# Revit family: Rinnai VT26  - face based
name_source: partatom
category: Plumbing Fixtures
revit_build: Autodesk Revit 2018 (Build: 20170223_1515(x64)
units: mm (PartAtom-declared; Revit-internal decimal feet)

## family parameters
Cut with Voids When Loaded = No
Host = Face
Part Type = Normal
Room Calculation Point = No
Round Connector Dimension = Use Diameter
Shared = No

## types (1)
- Rinnai VT26 External
    230 volt supply = 230 V
    CW Connection = Yes
    Cold Water Connection = Cold Water
    Cost = 1779 $
    Default Elevation = 1219 mm
    Description = Gas Califont Water Heater
    Gas Flow = 0.0 L/s
    Gas Supply Connection = Gas Supply - Copper
    HW Connection = Yes
    Hot Water Conection = Hot Water Out
    Keynote = 71-21
    Manufacturer = Rinnai
    Model = Infinity VT26  External
    Model Data = Colour       White
Input:       199 MJ/h or 55 kW
Output:     44.2 kW
Efficiency  80%   Energy Star Rating Up to 6.1

REU number: 	REU-VR2626WG
Factory preset temperature: 	55 °C
Rinnai product code 	INFVT26N/INFVT26L

Capacity 	Hot water capacity: 1.8 to 26 litres per minute
Nominal water capacity: 26 litres per minute at a 25 °C rise (1560 L/h)
Connections 	Hot water outlet: R¾ (20 mm)
Cold water inlet: R¾ (20 mm)

Gas supply: R¾ (20 mm)
Exhaust system 	Forced flue
Frost protection 	Fitted as standard.
Frost protection operates automatically, as long as the appliance is connected to the electrical power supply, by activating when the temperature inside the unit drops below 3.5 °C, and turns off once the temperature inside the unit reaches 7 °C.
Ignition system 	Direct electronic ignition
Injector size 	NG: 1.0, 1.55
LPG: 0.7, 1.05
Line pressure (min.) 	NG: 1.13 kPa, LPG 2.75 kPa
Line pressure (max.) 	3.5 kPa (maximum standing pressure under abnormal intermittent conditions is 5.0 kPa).

In the case of commercial metering, (i.e. 35-37 kPa coming in), there may be a requirement to regulate the incoming pressure down).
Power consumption 	Normal: 54 W (NG), 59 W (LPG), Standby: 2 W, Automatic Frost Protection: 125 W
Pressure relief 	Valve opens at 2060 kPa, valve closes at 1479 kPa

Noise level 	50 dB(A)
NOx af 	Less than 60 ppm
Safety devices 	Flame failure, boil-dry protection, overheat protection, fusible link, pressure relief valve and combustion fan rpm check
Water supply 	Nominal operating pressure: 130-1000 kPa
Activation flow rate: 2.4 litres per minute

Weight 	17 kg

Compliance 	ES: Supplier Declaration of Compliance
• Declaration Number: 12409201012
• Certificate Number: 6930
Market release 	2011
    Model Text mat = Rinnai Red Font
    Rinnai case finish = Rinnai Case White
    Type Comments = Input 199 MJ/h or 55 kW       Output 44.2kw
    Type Image = Rinnai VT26 gas califont.jpg
    URL = https://rinnai.co.nz
    Vent Connection = No
    Waste Connection = No
    Water Flow = 0.0 L/s

## geometry (parser evidence)
native form markers: Sweep x5
no freeform markers — native parametric forms only
